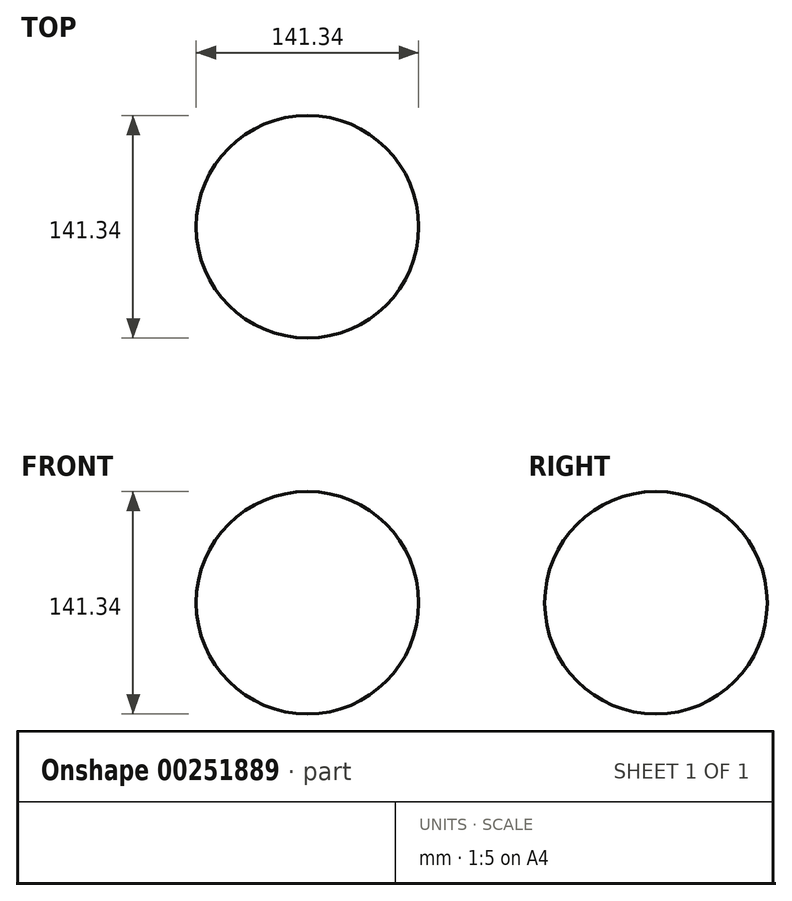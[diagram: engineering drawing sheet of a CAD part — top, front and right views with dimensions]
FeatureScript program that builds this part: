
annotation { "Feature Type Name" : "Feature", "Feature Type Description" : "" }
export const myFeature = defineFeature(function(context is Context, id is Id, definition is map)
    precondition{}
    {
        {
            var Q0;
            Q0=qCreatedBy(makeId("Front.planeOp"),FACE);
            var sketch = newSketch(context, id + "F0", { "sketchPlane" : qUnion([Q0])});
            skLineSegment(sketch, "E0", {"start": v(0, 82.66) * mm, "end": v(0, -95) * mm, "construction": true});
            skArc(sketch, "E1", {"start": v(0, 70.67) * mm, "mid": v(-70.67, 0) * mm, "end": v(0, -70.67) * mm});
            skLineSegment(sketch, "E2", {"start": v(0, -70.67) * mm, "end": v(0, 70.67) * mm});
            skSolve(sketch);
        }
        {
            var Q0;
            Q0=sQuery(id+"F0.wireOp",EDGE,"E1");
            var Q1;
            Q1=sQuery(id+"F0.wireOp",EDGE,"E2");
            revolve(context, id + "F1", {"bodyType" : ToolBodyType.SURFACE, "surfaceEntities" : qUnion([Q0]), "axis" : qUnion([Q1]), "revolveType" : RevolveType.FULL});
        }
    });
